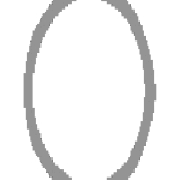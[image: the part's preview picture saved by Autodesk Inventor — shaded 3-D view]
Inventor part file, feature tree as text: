
AUTODESK INVENTOR PART (.ipt)
format: ipt  version: 2021 (Build 250183000, 183)  size: 113,664 bytes
history: native  units: in
note: dims shown in document units (in); Inventor stores cm internally (conversion verified against a paired STEP export)
features: other x4, sketch x3, plane x1
ambient origin geometry x8: Origin, YZ Plane, XZ Plane, XY Plane, X Axis, Y Axis, Z Axis, Center Point
bodies: Solid1 (feature_tree), Body (feature_tree)
feature tree (8):
  other  "Driven Length"
  other  "Frame Generator"
  other  "Start Plane"
  other  "End Plane"
  sketch  "Sketch"  dims[d2=15.625in d4=-0.0in d5=15.625in d6=0.12in d7=0.0in d8=90.0deg d9=15.625in]
  sketch  "Sketch2"  dims[d0=1.0in]
  plane  "Work Plane3"
  sketch  "Sketch3"  dims[d1=0.065in]
